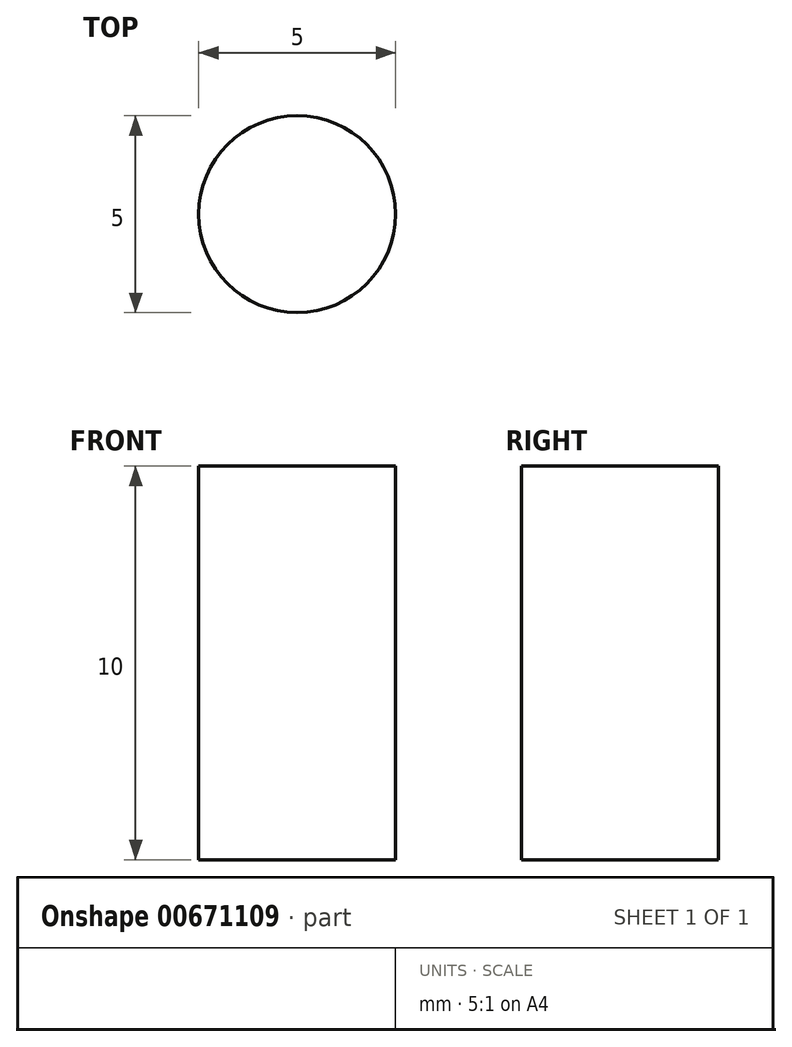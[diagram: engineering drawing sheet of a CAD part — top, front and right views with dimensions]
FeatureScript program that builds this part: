
annotation { "Feature Type Name" : "Feature", "Feature Type Description" : "" }
export const myFeature = defineFeature(function(context is Context, id is Id, definition is map)
    precondition{}
    {
        {
            var Q0;
            Q0=qCreatedBy(makeId("Top.planeOp"),FACE);
            var sketch = newSketch(context, id + "F0", { "sketchPlane" : qUnion([Q0])});
            skCircle(sketch, "E0", {"center": v(0, 0) * mm, "radius": 2.5 * mm});
            skSolve(sketch);
        }
        {
            var Q0;
            Q0=qSketchRegion(id+"F0",true);
            extrude(context, id + "F1", {"entities" : qUnion([Q0]), "depth" : 10 * mm});
        }
    });
